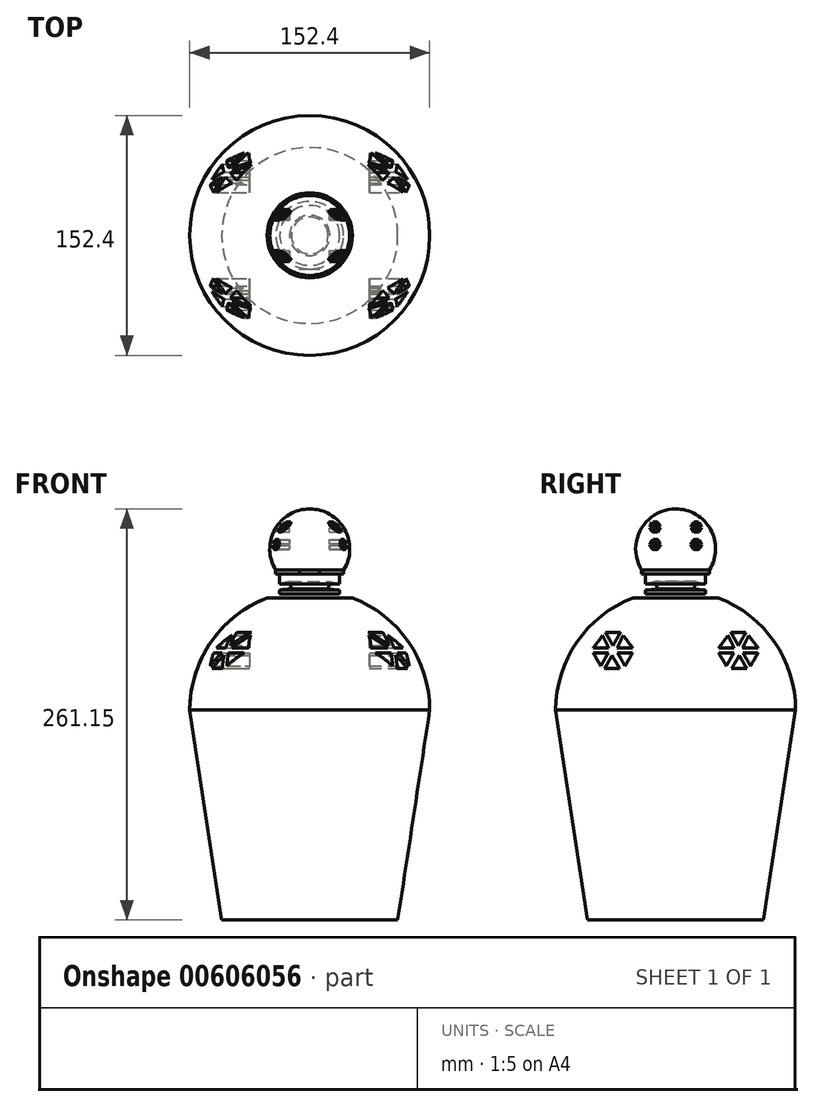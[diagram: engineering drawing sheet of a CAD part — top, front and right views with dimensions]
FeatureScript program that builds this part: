
annotation { "Feature Type Name" : "Feature", "Feature Type Description" : "" }
export const myFeature = defineFeature(function(context is Context, id is Id, definition is map)
    precondition{}
    {
        {
            var Q0;
            Q0=qCreatedBy(makeId("Right.planeOp"),FACE);
            var sketch = newSketch(context, id + "F0", { "sketchPlane" : qUnion([Q0])});
            skLineSegment(sketch, "E0", {"start": v(0, 0) * mm, "end": v(-76.2, 0) * mm});
            skLineSegment(sketch, "E1", {"start": v(0, 0) * mm, "end": v(76.2, 0) * mm});
            skArc(sketch, "E2", {"start": v(76.2, 0) * mm, "mid": v(0, 76.2) * mm, "end": v(-76.2, 0) * mm});
            skLineSegment(sketch, "E3", {"start": v(-19.05, 73.78) * mm, "end": v(19.05, 73.78) * mm});
            skLineSegment(sketch, "E4", {"start": v(-19.05, 73.78) * mm, "end": v(-19.05, 86.48) * mm});
            skLineSegment(sketch, "E5", {"start": v(-19.05, 86.48) * mm, "end": v(19.05, 86.48) * mm});
            skLineSegment(sketch, "E6", {"start": v(19.05, 86.48) * mm, "end": v(19.05, 73.78) * mm});
            skLineSegment(sketch, "E7", {"start": v(-19.05, 80.13) * mm, "end": v(-19.05, 76.32) * mm});
            skLineSegment(sketch, "E8", {"start": v(-19.05, 86.48) * mm, "end": v(-21.6, 86.48) * mm});
            skLineSegment(sketch, "E9", {"start": v(-21.6, 86.48) * mm, "end": v(-21.6, 89.02) * mm});
            skLineSegment(sketch, "E10", {"start": v(-21.6, 89.02) * mm, "end": v(21.59, 89.02) * mm});
            skLineSegment(sketch, "E11", {"start": v(21.59, 89.02) * mm, "end": v(21.59, 86.48) * mm});
            skLineSegment(sketch, "E12", {"start": v(21.59, 86.48) * mm, "end": v(19.05, 86.48) * mm});
            skArc(sketch, "E13", {"start": v(21.59, 89.02) * mm, "mid": v(0, 127.8) * mm, "end": v(-21.6, 89.02) * mm});
            skFitSpline(sketch, "E14", {"points": [v(-19.05, 80.13) * mm, v(-35.52, 80.13) * mm, v(-45.74, 88.7) * mm, v(-45.02, 104.83) * mm, v(-33.36, 105.83) * mm, v(-27.32, 90.87) * mm, v(-21.6, 86.48) * mm], "startDerivative": vector(-93.4, -10.6) * mm, "endDerivative": vector(53.06, -21.54) * mm});
            skFitSpline(sketch, "E15", {"points": [v(-19.05, 76.32) * mm, v(-39.12, 76.32) * mm, v(-50.81, 89.03) * mm, v(-48.47, 106.7) * mm, v(-31.02, 109.62) * mm, v(-26.22, 94.73) * mm, v(-21.6, 89.02) * mm], "startDerivative": vector(-113.52, -14.07) * mm, "endDerivative": vector(62.51, -36.47) * mm});
            skLineSegment(sketch, "E16", {"start": v(-27.04, 71.24) * mm, "end": v(27.04, 71.24) * mm});
            skLineSegment(sketch, "E17", {"start": v(0, 0) * mm, "end": v(0, 127.8) * mm});
            skLineSegment(sketch, "E18", {"start": v(-19.05, 80.13) * mm, "end": v(-12.8, 81.65) * mm});
            skLineSegment(sketch, "E19", {"start": v(-12.8, 81.65) * mm, "end": v(-11.67, 77) * mm});
            skLineSegment(sketch, "E20", {"start": v(-11.67, 77) * mm, "end": v(-19.05, 76.32) * mm});
            skLineSegment(sketch, "E21", {"start": v(-21.6, 89.02) * mm, "end": v(-16.42, 87.75) * mm});
            skPoint(sketch, "E21.endSnap0", {"position": v(-21.6, 87.75) * mm});
            skLineSegment(sketch, "E22", {"start": v(-16.42, 87.75) * mm, "end": v(-21.6, 86.48) * mm});
            skSolve(sketch);
        }
        {
            var Q0;
            {var subQ0=sQuery(id+"F0.wireOp",EDGE,"E0");Q0=makeQuery(id+"F0.imprint","IMPRINT",FACE,{"disambiguationData":[TD([[makeQuery(id+"F0.imprint","IMPRINT",EDGE,{"derivedFrom":subQ0}),-1.0]])]});}
            var Q1;
            {var subQ0=sQuery(id+"F0.wireOp",EDGE,"E13");var subQ3=sQuery(id+"F0.wireOp",EDGE,"E17");var subQ5=makeQuery(id+"F0.imprint","INTERSECT",VERTEX,{"derivedFrom":[subQ0,subQ3]});Q1=makeQuery(id+"F0.imprint","IMPRINT",FACE,{"disambiguationData":[TD([[makeQuery(id+"F0.imprint","IMPRINT",EDGE,{"disambiguationData":[TD([[subQ5,1.0]])],"derivedFrom":subQ3}),1.0]])]});}
            var Q2;
            {var subQ1=sQuery(id+"F0.wireOp",EDGE,"E2");var subQ3=sQuery(id+"F0.wireOp",EDGE,"E17");var subQ4=makeQuery(id+"F0.imprint","INTERSECT",VERTEX,{"derivedFrom":[subQ1,subQ3]});Q2=makeQuery(id+"F0.imprint","IMPRINT",FACE,{"disambiguationData":[TD([[makeQuery(id+"F0.imprint","IMPRINT",EDGE,{"disambiguationData":[TD([[subQ4,1.0]])],"derivedFrom":subQ3}),1.0]])]});}
            var Q3;
            {var subQ1=sQuery(id+"F0.wireOp",EDGE,"E2");var subQ3=sQuery(id+"F0.wireOp",EDGE,"E16");var subQ4=makeQuery(id+"F0.imprint","INTERSECT",VERTEX,{"disambiguationData":[OD(0.0)],"derivedFrom":[subQ1,subQ3]});Q3=makeQuery(id+"F0.imprint","IMPRINT",FACE,{"disambiguationData":[TD([[makeQuery(id+"F0.imprint","IMPRINT",EDGE,{"disambiguationData":[TD([[subQ4,-1.0]])],"derivedFrom":subQ3}),1.0]])]});}
            var Q4;
            {var subQ4=sQuery(id+"F0.wireOp",EDGE,"E8");Q4=makeQuery(id+"F0.imprint","IMPRINT",FACE,{"disambiguationData":[TD([[makeQuery(id+"F0.imprint","IMPRINT",EDGE,{"derivedFrom":subQ4}),-1.0]])]});}
            var Q5;
            {var subQ5=sQuery(id+"F0.wireOp",EDGE,"E18");Q5=makeQuery(id+"F0.imprint","IMPRINT",FACE,{"disambiguationData":[TD([[makeQuery(id+"F0.imprint","IMPRINT",EDGE,{"derivedFrom":subQ5}),1.0]])]});}
            var Q6;
            Q6=makeQuery(id+"F0.imprint","IMPRINT",FACE,{"disambiguationData":[TD([[makeQuery(id+"F0.imprint","IMPRINT",EDGE,{"derivedFrom":sQuery(id+"F0.wireOp",EDGE,"E7")}),1.0]])]});
            var Q7;
            Q7=makeQuery(id+"F0.imprint","IMPRINT",FACE,{"disambiguationData":[TD([[makeQuery(id+"F0.imprint","IMPRINT",EDGE,{"derivedFrom":sQuery(id+"F0.wireOp",EDGE,"E9")}),-1.0]])]});
            var Q8;
            Q8=sQuery(id+"F0.wireOp",EDGE,"E17");
            revolve(context, id + "F1", {"entities" : qUnion([Q0, Q1, Q2, Q3, Q4, Q5, Q6, Q7]), "axis" : qUnion([Q8]), "revolveType" : RevolveType.FULL});
        }
        {
            var Q0;
            Q0=makeQuery(id+"F0.imprint","IMPRINT",FACE,{"disambiguationData":[TD([[makeQuery(id+"F0.imprint","IMPRINT",EDGE,{"derivedFrom":sQuery(id+"F0.wireOp",EDGE,"E7")}),-1.0]])]});
            var Q1;
            Q1=makeQuery(id+"F0.imprint","IMPRINT",FACE,{"disambiguationData":[TD([[makeQuery(id+"F0.imprint","IMPRINT",EDGE,{"derivedFrom":sQuery(id+"F0.wireOp",EDGE,"E7")}),1.0]])]});
            var Q2;
            Q2=makeQuery(id+"F0.imprint","IMPRINT",FACE,{"disambiguationData":[TD([[makeQuery(id+"F0.imprint","IMPRINT",EDGE,{"derivedFrom":sQuery(id+"F0.wireOp",EDGE,"E9")}),-1.0]])]});
            extrude(context, id + "F2", {"entities" : qUnion([Q0, Q1, Q2]), "operationType" : NewBodyOperationType.ADD, "endBound" : BoundingType.SYMMETRIC, "depth" : 12.7 * mm, "offsetDistance" : 25.4 * mm});
        }
        {
            var Q0;
            Q0=qCreatedBy(makeId("Right.planeOp"),FACE);
            var sketch = newSketch(context, id + "F3", { "sketchPlane" : qUnion([Q0])});
            skLineSegment(sketch, "E23.0", {"start": v(0, 0) * mm, "end": v(-76.2, 0) * mm});
            skLineSegment(sketch, "E23.1", {"start": v(0, 0) * mm, "end": v(76.2, 0) * mm});
            skLineSegment(sketch, "E24", {"start": v(0, 0) * mm, "end": v(0, -133.35) * mm});
            skLineSegment(sketch, "E25", {"start": v(0, -133.35) * mm, "end": v(-55.88, -133.35) * mm});
            skLineSegment(sketch, "E26", {"start": v(-55.88, -133.35) * mm, "end": v(-76.2, 0) * mm});
            skSolve(sketch);
        }
        {
            var Q0;
            Q0 = qSketchRegion(id + "F3", true);
            var Q1;
            Q1=sQuery(id+"F3.wireOp",EDGE,"E24");
            revolve(context, id + "F4", {"entities" : qUnion([Q0]), "axis" : qUnion([Q1]), "revolveType" : RevolveType.FULL});
        }
        {
            var Q0;
            Q0=qCreatedBy(makeId("Right.planeOp"),FACE);
            var sketch = newSketch(context, id + "F5", { "sketchPlane" : qUnion([Q0])});
            skLineSegment(sketch, "E27.0", {"start": v(76.2, 0) * mm, "end": v(-76.2, 0) * mm});
            skLineSegment(sketch, "E28.0", {"start": v(19.05, 73.78) * mm, "end": v(-19.05, 73.78) * mm});
            skLineSegment(sketch, "E29", {"start": v(0, 73.78) * mm, "end": v(0, 0) * mm, "construction": true});
            skLineSegment(sketch, "E30", {"start": v(-45.22, 26.32) * mm, "end": v(-35.57, 26.32) * mm});
            skLineSegment(sketch, "E31", {"start": v(-35.57, 26.32) * mm, "end": v(-40.4, 34.68) * mm});
            skPoint(sketch, "E31.endSnap0", {"position": v(-40.4, 26.32) * mm});
            skLineSegment(sketch, "E32", {"start": v(-40.4, 34.68) * mm, "end": v(-45.22, 26.32) * mm});
            skCircle(sketch, "E33", {"center": v(-39.84, 37.8) * mm, "radius": 3.18 * mm, "construction": true});
            skLineSegment(sketch, "E34", {"start": v(-39.84, 40.98) * mm, "end": v(-44.67, 49.35) * mm});
            skLineSegment(sketch, "E35", {"start": v(-44.67, 49.35) * mm, "end": v(-35.01, 49.35) * mm});
            skLineSegment(sketch, "E36", {"start": v(-35.01, 49.35) * mm, "end": v(-39.84, 40.98) * mm});
            skLineSegment(sketch, "E37", {"start": v(-42.7, 36.43) * mm, "end": v(-47.53, 28.07) * mm});
            skLineSegment(sketch, "E38", {"start": v(-47.53, 28.07) * mm, "end": v(-52.36, 36.43) * mm});
            skLineSegment(sketch, "E39", {"start": v(-52.36, 36.43) * mm, "end": v(-42.7, 36.43) * mm});
            skLineSegment(sketch, "E40", {"start": v(-42.54, 39.48) * mm, "end": v(-52.36, 39.48) * mm});
            skLineSegment(sketch, "E41", {"start": v(-52.36, 39.48) * mm, "end": v(-46.36, 47.41) * mm});
            skLineSegment(sketch, "E42", {"start": v(-46.36, 47.41) * mm, "end": v(-42.54, 39.48) * mm});
            skLineSegment(sketch, "E43.MirrorCS", {"start": v(-36.98, 36.43) * mm, "end": v(-32.15, 28.07) * mm});
            skLineSegment(sketch, "E44.MirrorCS", {"start": v(-32.15, 28.07) * mm, "end": v(-27.32, 36.43) * mm});
            skLineSegment(sketch, "E45.MirrorCS", {"start": v(-27.32, 36.43) * mm, "end": v(-36.98, 36.43) * mm});
            skLineSegment(sketch, "E46.MirrorCS", {"start": v(-37.14, 39.48) * mm, "end": v(-27.32, 39.48) * mm});
            skLineSegment(sketch, "E47.MirrorCS", {"start": v(-33.32, 47.41) * mm, "end": v(-37.14, 39.48) * mm});
            skLineSegment(sketch, "E48.MirrorCS", {"start": v(-27.32, 39.48) * mm, "end": v(-33.32, 47.41) * mm});
            skCircle(sketch, "E49.MirrorC", {"center": v(39.84, 37.8) * mm, "radius": 3.18 * mm, "construction": true});
            skLineSegment(sketch, "E50.MirrorCS", {"start": v(45.22, 26.32) * mm, "end": v(35.57, 26.32) * mm});
            skLineSegment(sketch, "E51.MirrorCS", {"start": v(46.36, 47.41) * mm, "end": v(42.54, 39.48) * mm});
            skLineSegment(sketch, "E52.MirrorCS", {"start": v(37.14, 39.48) * mm, "end": v(27.32, 39.48) * mm});
            skLineSegment(sketch, "E53.MirrorCS", {"start": v(44.67, 49.35) * mm, "end": v(35.01, 49.35) * mm});
            skLineSegment(sketch, "E54.MirrorCS", {"start": v(52.36, 36.43) * mm, "end": v(42.7, 36.43) * mm});
            skLineSegment(sketch, "E55.MirrorCS", {"start": v(39.84, 40.98) * mm, "end": v(44.67, 49.35) * mm});
            skLineSegment(sketch, "E56.MirrorCS", {"start": v(42.54, 39.48) * mm, "end": v(52.36, 39.48) * mm});
            skLineSegment(sketch, "E57.MirrorCS", {"start": v(35.01, 49.35) * mm, "end": v(39.84, 40.98) * mm});
            skLineSegment(sketch, "E58.MirrorCS", {"start": v(42.7, 36.43) * mm, "end": v(47.53, 28.07) * mm});
            skLineSegment(sketch, "E59.MirrorCS", {"start": v(33.32, 47.41) * mm, "end": v(37.14, 39.48) * mm});
            skLineSegment(sketch, "E60.MirrorCS", {"start": v(35.57, 26.32) * mm, "end": v(40.4, 34.68) * mm});
            skLineSegment(sketch, "E61.MirrorCS", {"start": v(47.53, 28.07) * mm, "end": v(52.36, 36.43) * mm});
            skLineSegment(sketch, "E62.MirrorCS", {"start": v(27.32, 36.43) * mm, "end": v(36.98, 36.43) * mm});
            skLineSegment(sketch, "E63.MirrorCS", {"start": v(32.15, 28.07) * mm, "end": v(27.32, 36.43) * mm});
            skLineSegment(sketch, "E64.MirrorCS", {"start": v(27.32, 39.48) * mm, "end": v(33.32, 47.41) * mm});
            skPoint(sketch, "E65.MirrorP", {"position": v(40.4, 26.32) * mm});
            skLineSegment(sketch, "E66.MirrorCS", {"start": v(52.36, 39.48) * mm, "end": v(46.36, 47.41) * mm});
            skLineSegment(sketch, "E67.MirrorCS", {"start": v(40.4, 34.68) * mm, "end": v(45.22, 26.32) * mm});
            skLineSegment(sketch, "E68.MirrorCS", {"start": v(36.98, 36.43) * mm, "end": v(32.15, 28.07) * mm});
            skSolve(sketch);
        }
        {
            var Q0;
            Q0 = qSketchRegion(id + "F5", true);
            extrude(context, id + "F6", {"entities" : qUnion([Q0]), "operationType" : NewBodyOperationType.ADD, "endBound" : BoundingType.SYMMETRIC, "depth" : 101.6 * mm, "offsetDistance" : 25.4 * mm, "hasSecondDirection" : true, "secondDirectionOppositeDirection" : true, "secondDirectionDepth" : 25.4 * mm});
        }
        {
            var Q0;
            Q0 = qSketchRegion(id + "F5", true);
            extrude(context, id + "F7", {"entities" : qUnion([Q0]), "operationType" : NewBodyOperationType.ADD, "endBound" : BoundingType.SYMMETRIC, "depth" : 127 * mm, "offsetDistance" : 25.4 * mm});
        }
        {
            var Q0;
            Q0=makeQuery(id+"F7.opExtrude","CAP_FACE",FACE,{"disambiguationData":[OSD([sQuery(id+"F5.wireOp",EDGE,"E40"),sQuery(id+"F5.wireOp",EDGE,"E41"),sQuery(id+"F5.wireOp",EDGE,"E42")])],"isStart":false});
            var Q1;
            Q1=makeQuery(id+"F7.opExtrude","CAP_FACE",FACE,{"disambiguationData":[OSD([sQuery(id+"F5.wireOp",EDGE,"E34"),sQuery(id+"F5.wireOp",EDGE,"E35"),sQuery(id+"F5.wireOp",EDGE,"E36")])],"isStart":false});
            var Q2;
            Q2=makeQuery(id+"F7.opExtrude","CAP_FACE",FACE,{"disambiguationData":[OSD([sQuery(id+"F5.wireOp",EDGE,"E46.MirrorCS"),sQuery(id+"F5.wireOp",EDGE,"E47.MirrorCS"),sQuery(id+"F5.wireOp",EDGE,"E48.MirrorCS")])],"isStart":false});
            var Q3;
            Q3=makeQuery(id+"F7.opExtrude","CAP_FACE",FACE,{"disambiguationData":[OSD([sQuery(id+"F5.wireOp",EDGE,"E43.MirrorCS"),sQuery(id+"F5.wireOp",EDGE,"E44.MirrorCS"),sQuery(id+"F5.wireOp",EDGE,"E45.MirrorCS")])],"isStart":false});
            var Q4;
            Q4=makeQuery(id+"F7.opExtrude","CAP_FACE",FACE,{"disambiguationData":[OSD([sQuery(id+"F5.wireOp",EDGE,"E30"),sQuery(id+"F5.wireOp",EDGE,"E31"),sQuery(id+"F5.wireOp",EDGE,"E32")])],"isStart":false});
            var Q5;
            Q5=makeQuery(id+"F7.opExtrude","CAP_FACE",FACE,{"disambiguationData":[OSD([sQuery(id+"F5.wireOp",EDGE,"E37"),sQuery(id+"F5.wireOp",EDGE,"E38"),sQuery(id+"F5.wireOp",EDGE,"E39")])],"isStart":false});
            var Q6;
            Q6=makeQuery(id+"F7.opExtrude","CAP_FACE",FACE,{"disambiguationData":[OSD([sQuery(id+"F5.wireOp",EDGE,"E62.MirrorCS"),sQuery(id+"F5.wireOp",EDGE,"E63.MirrorCS"),sQuery(id+"F5.wireOp",EDGE,"E68.MirrorCS")])],"isStart":false});
            var Q7;
            Q7=makeQuery(id+"F7.opExtrude","CAP_FACE",FACE,{"disambiguationData":[OSD([sQuery(id+"F5.wireOp",EDGE,"E52.MirrorCS"),sQuery(id+"F5.wireOp",EDGE,"E59.MirrorCS"),sQuery(id+"F5.wireOp",EDGE,"E64.MirrorCS")])],"isStart":false});
            var Q8;
            Q8=makeQuery(id+"F7.opExtrude","CAP_FACE",FACE,{"disambiguationData":[OSD([sQuery(id+"F5.wireOp",EDGE,"E53.MirrorCS"),sQuery(id+"F5.wireOp",EDGE,"E55.MirrorCS"),sQuery(id+"F5.wireOp",EDGE,"E57.MirrorCS")])],"isStart":false});
            var Q9;
            Q9=makeQuery(id+"F7.opExtrude","CAP_FACE",FACE,{"disambiguationData":[OSD([sQuery(id+"F5.wireOp",EDGE,"E51.MirrorCS"),sQuery(id+"F5.wireOp",EDGE,"E56.MirrorCS"),sQuery(id+"F5.wireOp",EDGE,"E66.MirrorCS")])],"isStart":false});
            var Q10;
            Q10=makeQuery(id+"F7.opExtrude","CAP_FACE",FACE,{"disambiguationData":[OSD([sQuery(id+"F5.wireOp",EDGE,"E54.MirrorCS"),sQuery(id+"F5.wireOp",EDGE,"E58.MirrorCS"),sQuery(id+"F5.wireOp",EDGE,"E61.MirrorCS")])],"isStart":false});
            var Q11;
            Q11=makeQuery(id+"F7.opExtrude","CAP_FACE",FACE,{"disambiguationData":[OSD([sQuery(id+"F5.wireOp",EDGE,"E50.MirrorCS"),sQuery(id+"F5.wireOp",EDGE,"E60.MirrorCS"),sQuery(id+"F5.wireOp",EDGE,"E67.MirrorCS")])],"isStart":false});
            var Q12;
            Q12=makeQuery(id+"F7.opExtrude","CAP_FACE",FACE,{"disambiguationData":[OSD([sQuery(id+"F5.wireOp",EDGE,"E51.MirrorCS"),sQuery(id+"F5.wireOp",EDGE,"E56.MirrorCS"),sQuery(id+"F5.wireOp",EDGE,"E66.MirrorCS")])],"isStart":true});
            var Q13;
            Q13=makeQuery(id+"F7.opExtrude","CAP_FACE",FACE,{"disambiguationData":[OSD([sQuery(id+"F5.wireOp",EDGE,"E54.MirrorCS"),sQuery(id+"F5.wireOp",EDGE,"E58.MirrorCS"),sQuery(id+"F5.wireOp",EDGE,"E61.MirrorCS")])],"isStart":true});
            var Q14;
            Q14=makeQuery(id+"F7.opExtrude","CAP_FACE",FACE,{"disambiguationData":[OSD([sQuery(id+"F5.wireOp",EDGE,"E50.MirrorCS"),sQuery(id+"F5.wireOp",EDGE,"E60.MirrorCS"),sQuery(id+"F5.wireOp",EDGE,"E67.MirrorCS")])],"isStart":true});
            var Q15;
            Q15=makeQuery(id+"F7.opExtrude","CAP_FACE",FACE,{"disambiguationData":[OSD([sQuery(id+"F5.wireOp",EDGE,"E62.MirrorCS"),sQuery(id+"F5.wireOp",EDGE,"E63.MirrorCS"),sQuery(id+"F5.wireOp",EDGE,"E68.MirrorCS")])],"isStart":true});
            var Q16;
            Q16=makeQuery(id+"F7.opExtrude","CAP_FACE",FACE,{"disambiguationData":[OSD([sQuery(id+"F5.wireOp",EDGE,"E52.MirrorCS"),sQuery(id+"F5.wireOp",EDGE,"E59.MirrorCS"),sQuery(id+"F5.wireOp",EDGE,"E64.MirrorCS")])],"isStart":true});
            var Q17;
            Q17=makeQuery(id+"F7.opExtrude","CAP_FACE",FACE,{"disambiguationData":[OSD([sQuery(id+"F5.wireOp",EDGE,"E53.MirrorCS"),sQuery(id+"F5.wireOp",EDGE,"E55.MirrorCS"),sQuery(id+"F5.wireOp",EDGE,"E57.MirrorCS")])],"isStart":true});
            var Q18;
            Q18=makeQuery(id+"F7.opExtrude","CAP_FACE",FACE,{"disambiguationData":[OSD([sQuery(id+"F5.wireOp",EDGE,"E43.MirrorCS"),sQuery(id+"F5.wireOp",EDGE,"E44.MirrorCS"),sQuery(id+"F5.wireOp",EDGE,"E45.MirrorCS")])],"isStart":true});
            var Q19;
            Q19=makeQuery(id+"F7.opExtrude","CAP_FACE",FACE,{"disambiguationData":[OSD([sQuery(id+"F5.wireOp",EDGE,"E30"),sQuery(id+"F5.wireOp",EDGE,"E31"),sQuery(id+"F5.wireOp",EDGE,"E32")])],"isStart":true});
            var Q20;
            Q20=makeQuery(id+"F7.opExtrude","CAP_FACE",FACE,{"disambiguationData":[OSD([sQuery(id+"F5.wireOp",EDGE,"E37"),sQuery(id+"F5.wireOp",EDGE,"E38"),sQuery(id+"F5.wireOp",EDGE,"E39")])],"isStart":true});
            var Q21;
            Q21=makeQuery(id+"F7.opExtrude","CAP_FACE",FACE,{"disambiguationData":[OSD([sQuery(id+"F5.wireOp",EDGE,"E40"),sQuery(id+"F5.wireOp",EDGE,"E41"),sQuery(id+"F5.wireOp",EDGE,"E42")])],"isStart":true});
            var Q22;
            Q22=makeQuery(id+"F7.opExtrude","CAP_FACE",FACE,{"disambiguationData":[OSD([sQuery(id+"F5.wireOp",EDGE,"E34"),sQuery(id+"F5.wireOp",EDGE,"E35"),sQuery(id+"F5.wireOp",EDGE,"E36")])],"isStart":true});
            var Q23;
            Q23=makeQuery(id+"F7.opExtrude","CAP_FACE",FACE,{"disambiguationData":[OSD([sQuery(id+"F5.wireOp",EDGE,"E46.MirrorCS"),sQuery(id+"F5.wireOp",EDGE,"E47.MirrorCS"),sQuery(id+"F5.wireOp",EDGE,"E48.MirrorCS")])],"isStart":true});
            extrude(context, id + "F8", {"entities" : qUnion([Q0, Q1, Q2, Q3, Q4, Q5, Q6, Q7, Q8, Q9, Q10, Q11, Q12, Q13, Q14, Q15, Q16, Q17, Q18, Q19, Q20, Q21, Q22, Q23]), "operationType" : NewBodyOperationType.REMOVE, "oppositeDirection" : true, "depth" : 25.4 * mm, "offsetDistance" : 25.4 * mm, "hasSecondDirection" : true, "secondDirectionOppositeDirection" : false, "secondDirectionDepth" : 25.4 * mm});
        }
        {
            var Q0;
            Q0=qCreatedBy(makeId("Right.planeOp"),FACE);
            var sketch = newSketch(context, id + "F9", { "sketchPlane" : qUnion([Q0])});
            skLineSegment(sketch, "E69.0", {"start": v(21.59, 89.02) * mm, "end": v(-21.6, 89.02) * mm});
            skLineSegment(sketch, "E70", {"start": v(0, 89.02) * mm, "end": v(0, 127.8) * mm, "construction": true});
            skLineSegment(sketch, "E71", {"start": v(-13.1, 116.83) * mm, "end": v(-14.54, 119.33) * mm});
            skLineSegment(sketch, "E72", {"start": v(-14.54, 119.33) * mm, "end": v(-11.65, 119.33) * mm});
            skLineSegment(sketch, "E73", {"start": v(-11.65, 119.33) * mm, "end": v(-13.1, 116.83) * mm});
            skLineSegment(sketch, "E74", {"start": v(-13.1, 115.56) * mm, "end": v(-14.54, 113.05) * mm});
            skLineSegment(sketch, "E75", {"start": v(-14.54, 113.05) * mm, "end": v(-11.65, 113.05) * mm});
            skLineSegment(sketch, "E76", {"start": v(-11.65, 113.05) * mm, "end": v(-13.1, 115.56) * mm});
            skLineSegment(sketch, "E77", {"start": v(-13.58, 115.79) * mm, "end": v(-15.03, 113.28) * mm});
            skLineSegment(sketch, "E78", {"start": v(-15.03, 113.28) * mm, "end": v(-16.47, 115.79) * mm});
            skLineSegment(sketch, "E79", {"start": v(-16.47, 115.79) * mm, "end": v(-13.58, 115.79) * mm});
            skLineSegment(sketch, "E80", {"start": v(-13.58, 116.6) * mm, "end": v(-16.47, 116.6) * mm});
            skLineSegment(sketch, "E81", {"start": v(-16.47, 116.6) * mm, "end": v(-15.03, 119.1) * mm});
            skLineSegment(sketch, "E82", {"start": v(-15.03, 119.1) * mm, "end": v(-13.58, 116.6) * mm});
            skPoint(sketch, "E83.endSnap0", {"position": v(-13.1, 113.05) * mm});
            skLineSegment(sketch, "E84.MirrorCS", {"start": v(-11.16, 119.1) * mm, "end": v(-12.6, 116.6) * mm});
            skLineSegment(sketch, "E85.MirrorCS", {"start": v(-9.71, 116.6) * mm, "end": v(-11.16, 119.1) * mm});
            skLineSegment(sketch, "E86.MirrorCS", {"start": v(-12.6, 116.6) * mm, "end": v(-9.71, 116.6) * mm});
            skLineSegment(sketch, "E87.MirrorCS", {"start": v(-9.71, 115.79) * mm, "end": v(-12.6, 115.79) * mm});
            skLineSegment(sketch, "E88.MirrorCS", {"start": v(-12.6, 115.79) * mm, "end": v(-11.16, 113.28) * mm});
            skLineSegment(sketch, "E89.MirrorCS", {"start": v(-11.16, 113.28) * mm, "end": v(-9.71, 115.79) * mm});
            skLineSegment(sketch, "E90.MirrorCS", {"start": v(-14.54, 108.27) * mm, "end": v(-11.65, 108.27) * mm});
            skLineSegment(sketch, "E91.MirrorCS", {"start": v(-15.03, 108.04) * mm, "end": v(-16.47, 105.54) * mm});
            skLineSegment(sketch, "E92.MirrorCS", {"start": v(-13.58, 105.54) * mm, "end": v(-15.03, 108.04) * mm});
            skLineSegment(sketch, "E93.MirrorCS", {"start": v(-13.1, 105.77) * mm, "end": v(-14.54, 108.27) * mm});
            skLineSegment(sketch, "E94.MirrorCS", {"start": v(-11.65, 108.27) * mm, "end": v(-13.1, 105.77) * mm});
            skLineSegment(sketch, "E95.MirrorCS", {"start": v(-16.47, 105.54) * mm, "end": v(-13.58, 105.54) * mm});
            skLineSegment(sketch, "E96.MirrorCS", {"start": v(-12.6, 105.54) * mm, "end": v(-11.16, 108.04) * mm});
            skLineSegment(sketch, "E97.MirrorCS", {"start": v(-11.16, 108.04) * mm, "end": v(-9.71, 105.54) * mm});
            skLineSegment(sketch, "E98.MirrorCS", {"start": v(-9.71, 105.54) * mm, "end": v(-12.6, 105.54) * mm});
            skLineSegment(sketch, "E99.MirrorCS", {"start": v(-12.6, 104.73) * mm, "end": v(-9.71, 104.73) * mm});
            skLineSegment(sketch, "E100.MirrorCS", {"start": v(-9.71, 104.73) * mm, "end": v(-11.16, 102.22) * mm});
            skLineSegment(sketch, "E101.MirrorCS", {"start": v(-11.16, 102.22) * mm, "end": v(-12.6, 104.73) * mm});
            skLineSegment(sketch, "E102.MirrorCS", {"start": v(-11.65, 102) * mm, "end": v(-13.1, 104.5) * mm});
            skLineSegment(sketch, "E103.MirrorCS", {"start": v(-14.54, 102) * mm, "end": v(-11.65, 102) * mm});
            skLineSegment(sketch, "E104.MirrorCS", {"start": v(-13.1, 104.5) * mm, "end": v(-14.54, 102) * mm});
            skLineSegment(sketch, "E105.MirrorCS", {"start": v(-15.03, 102.22) * mm, "end": v(-13.58, 104.73) * mm});
            skLineSegment(sketch, "E106.MirrorCS", {"start": v(-13.58, 104.73) * mm, "end": v(-16.47, 104.73) * mm});
            skLineSegment(sketch, "E107.MirrorCS", {"start": v(-16.47, 104.73) * mm, "end": v(-15.03, 102.22) * mm});
            skLineSegment(sketch, "E108.MirrorCS", {"start": v(11.65, 113.05) * mm, "end": v(13.1, 115.56) * mm});
            skLineSegment(sketch, "E109.MirrorCS", {"start": v(13.1, 115.56) * mm, "end": v(14.54, 113.05) * mm});
            skLineSegment(sketch, "E110.MirrorCS", {"start": v(14.54, 113.05) * mm, "end": v(11.65, 113.05) * mm});
            skLineSegment(sketch, "E111.MirrorCS", {"start": v(11.65, 102) * mm, "end": v(13.1, 104.5) * mm});
            skLineSegment(sketch, "E112.MirrorCS", {"start": v(9.71, 116.6) * mm, "end": v(11.16, 119.1) * mm});
            skLineSegment(sketch, "E113.MirrorCS", {"start": v(12.6, 115.79) * mm, "end": v(11.16, 113.28) * mm});
            skLineSegment(sketch, "E114.MirrorCS", {"start": v(15.03, 119.1) * mm, "end": v(13.58, 116.6) * mm});
            skLineSegment(sketch, "E115.MirrorCS", {"start": v(15.03, 108.04) * mm, "end": v(16.47, 105.54) * mm});
            skLineSegment(sketch, "E116.MirrorCS", {"start": v(16.47, 104.73) * mm, "end": v(15.03, 102.22) * mm});
            skLineSegment(sketch, "E117.MirrorCS", {"start": v(13.1, 116.83) * mm, "end": v(14.54, 119.33) * mm});
            skLineSegment(sketch, "E118.MirrorCS", {"start": v(11.16, 113.28) * mm, "end": v(9.71, 115.79) * mm});
            skLineSegment(sketch, "E119.MirrorCS", {"start": v(16.47, 115.79) * mm, "end": v(13.58, 115.79) * mm});
            skPoint(sketch, "E120.MirrorP", {"position": v(13.1, 113.05) * mm});
            skLineSegment(sketch, "E121.MirrorCS", {"start": v(12.6, 105.54) * mm, "end": v(11.16, 108.04) * mm});
            skLineSegment(sketch, "E122.MirrorCS", {"start": v(13.58, 104.73) * mm, "end": v(16.47, 104.73) * mm});
            skLineSegment(sketch, "E123.MirrorCS", {"start": v(11.16, 108.04) * mm, "end": v(9.71, 105.54) * mm});
            skLineSegment(sketch, "E124.MirrorCS", {"start": v(11.16, 119.1) * mm, "end": v(12.6, 116.6) * mm});
            skLineSegment(sketch, "E125.MirrorCS", {"start": v(16.47, 105.54) * mm, "end": v(13.58, 105.54) * mm});
            skLineSegment(sketch, "E126.MirrorCS", {"start": v(9.71, 104.73) * mm, "end": v(11.16, 102.22) * mm});
            skLineSegment(sketch, "E127.MirrorCS", {"start": v(14.54, 108.27) * mm, "end": v(11.65, 108.27) * mm});
            skLineSegment(sketch, "E128.MirrorCS", {"start": v(9.71, 115.79) * mm, "end": v(12.6, 115.79) * mm});
            skLineSegment(sketch, "E129.MirrorCS", {"start": v(13.58, 115.79) * mm, "end": v(15.03, 113.28) * mm});
            skLineSegment(sketch, "E130.MirrorCS", {"start": v(14.54, 119.33) * mm, "end": v(11.65, 119.33) * mm});
            skLineSegment(sketch, "E131.MirrorCS", {"start": v(11.16, 102.22) * mm, "end": v(12.6, 104.73) * mm});
            skLineSegment(sketch, "E132.MirrorCS", {"start": v(14.54, 102) * mm, "end": v(11.65, 102) * mm});
            skLineSegment(sketch, "E133.MirrorCS", {"start": v(12.6, 104.73) * mm, "end": v(9.71, 104.73) * mm});
            skLineSegment(sketch, "E134.MirrorCS", {"start": v(15.03, 102.22) * mm, "end": v(13.58, 104.73) * mm});
            skLineSegment(sketch, "E135.MirrorCS", {"start": v(11.65, 108.27) * mm, "end": v(13.1, 105.77) * mm});
            skLineSegment(sketch, "E136.MirrorCS", {"start": v(16.47, 116.6) * mm, "end": v(15.03, 119.1) * mm});
            skLineSegment(sketch, "E137.MirrorCS", {"start": v(13.58, 116.6) * mm, "end": v(16.47, 116.6) * mm});
            skLineSegment(sketch, "E138.MirrorCS", {"start": v(12.6, 116.6) * mm, "end": v(9.71, 116.6) * mm});
            skLineSegment(sketch, "E139.MirrorCS", {"start": v(15.03, 113.28) * mm, "end": v(16.47, 115.79) * mm});
            skLineSegment(sketch, "E140.MirrorCS", {"start": v(11.65, 119.33) * mm, "end": v(13.1, 116.83) * mm});
            skLineSegment(sketch, "E141.MirrorCS", {"start": v(13.1, 104.5) * mm, "end": v(14.54, 102) * mm});
            skLineSegment(sketch, "E142.MirrorCS", {"start": v(13.1, 105.77) * mm, "end": v(14.54, 108.27) * mm});
            skLineSegment(sketch, "E143.MirrorCS", {"start": v(13.58, 105.54) * mm, "end": v(15.03, 108.04) * mm});
            skLineSegment(sketch, "E144.MirrorCS", {"start": v(9.71, 105.54) * mm, "end": v(12.6, 105.54) * mm});
            skSolve(sketch);
        }
        {
            var Q0;
            Q0 = qSketchRegion(id + "F9", true);
            extrude(context, id + "F10", {"entities" : qUnion([Q0]), "operationType" : NewBodyOperationType.ADD, "endBound" : BoundingType.SYMMETRIC, "depth" : 50.8 * mm, "offsetDistance" : 25.4 * mm});
        }
        {
            var Q0;
            Q0=makeQuery(id+"F10.opExtrude","CAP_FACE",FACE,{"disambiguationData":[OSD([sQuery(id+"F9.wireOp",EDGE,"E80"),sQuery(id+"F9.wireOp",EDGE,"E81"),sQuery(id+"F9.wireOp",EDGE,"E82")])],"isStart":false});
            var Q1;
            Q1=makeQuery(id+"F10.opExtrude","CAP_FACE",FACE,{"disambiguationData":[OSD([sQuery(id+"F9.wireOp",EDGE,"E71"),sQuery(id+"F9.wireOp",EDGE,"E72"),sQuery(id+"F9.wireOp",EDGE,"E73")])],"isStart":false});
            var Q2;
            Q2=makeQuery(id+"F10.opExtrude","CAP_FACE",FACE,{"disambiguationData":[OSD([sQuery(id+"F9.wireOp",EDGE,"E84.MirrorCS"),sQuery(id+"F9.wireOp",EDGE,"E85.MirrorCS"),sQuery(id+"F9.wireOp",EDGE,"E86.MirrorCS")])],"isStart":false});
            var Q3;
            Q3=makeQuery(id+"F10.opExtrude","CAP_FACE",FACE,{"disambiguationData":[OSD([sQuery(id+"F9.wireOp",EDGE,"E87.MirrorCS"),sQuery(id+"F9.wireOp",EDGE,"E88.MirrorCS"),sQuery(id+"F9.wireOp",EDGE,"E89.MirrorCS")])],"isStart":false});
            var Q4;
            Q4=makeQuery(id+"F10.opExtrude","CAP_FACE",FACE,{"disambiguationData":[OSD([sQuery(id+"F9.wireOp",EDGE,"E74"),sQuery(id+"F9.wireOp",EDGE,"E75"),sQuery(id+"F9.wireOp",EDGE,"E76")])],"isStart":false});
            var Q5;
            Q5=makeQuery(id+"F10.opExtrude","CAP_FACE",FACE,{"disambiguationData":[OSD([sQuery(id+"F9.wireOp",EDGE,"E77"),sQuery(id+"F9.wireOp",EDGE,"E78"),sQuery(id+"F9.wireOp",EDGE,"E79")])],"isStart":false});
            var Q6;
            Q6=makeQuery(id+"F10.opExtrude","CAP_FACE",FACE,{"disambiguationData":[OSD([sQuery(id+"F9.wireOp",EDGE,"E105.MirrorCS"),sQuery(id+"F9.wireOp",EDGE,"E106.MirrorCS"),sQuery(id+"F9.wireOp",EDGE,"E107.MirrorCS")])],"isStart":false});
            var Q7;
            Q7=makeQuery(id+"F10.opExtrude","CAP_FACE",FACE,{"disambiguationData":[OSD([sQuery(id+"F9.wireOp",EDGE,"E91.MirrorCS"),sQuery(id+"F9.wireOp",EDGE,"E92.MirrorCS"),sQuery(id+"F9.wireOp",EDGE,"E95.MirrorCS")])],"isStart":false});
            var Q8;
            Q8=makeQuery(id+"F10.opExtrude","CAP_FACE",FACE,{"disambiguationData":[OSD([sQuery(id+"F9.wireOp",EDGE,"E90.MirrorCS"),sQuery(id+"F9.wireOp",EDGE,"E93.MirrorCS"),sQuery(id+"F9.wireOp",EDGE,"E94.MirrorCS")])],"isStart":false});
            var Q9;
            Q9=makeQuery(id+"F10.opExtrude","CAP_FACE",FACE,{"disambiguationData":[OSD([sQuery(id+"F9.wireOp",EDGE,"E96.MirrorCS"),sQuery(id+"F9.wireOp",EDGE,"E97.MirrorCS"),sQuery(id+"F9.wireOp",EDGE,"E98.MirrorCS")])],"isStart":false});
            var Q10;
            Q10=makeQuery(id+"F10.opExtrude","CAP_FACE",FACE,{"disambiguationData":[OSD([sQuery(id+"F9.wireOp",EDGE,"E99.MirrorCS"),sQuery(id+"F9.wireOp",EDGE,"E100.MirrorCS"),sQuery(id+"F9.wireOp",EDGE,"E101.MirrorCS")])],"isStart":false});
            var Q11;
            Q11=makeQuery(id+"F10.opExtrude","CAP_FACE",FACE,{"disambiguationData":[OSD([sQuery(id+"F9.wireOp",EDGE,"E102.MirrorCS"),sQuery(id+"F9.wireOp",EDGE,"E103.MirrorCS"),sQuery(id+"F9.wireOp",EDGE,"E104.MirrorCS")])],"isStart":false});
            var Q12;
            Q12=makeQuery(id+"F10.opExtrude","CAP_FACE",FACE,{"disambiguationData":[OSD([sQuery(id+"F9.wireOp",EDGE,"E126.MirrorCS"),sQuery(id+"F9.wireOp",EDGE,"E131.MirrorCS"),sQuery(id+"F9.wireOp",EDGE,"E133.MirrorCS")])],"isStart":false});
            var Q13;
            Q13=makeQuery(id+"F10.opExtrude","CAP_FACE",FACE,{"disambiguationData":[OSD([sQuery(id+"F9.wireOp",EDGE,"E111.MirrorCS"),sQuery(id+"F9.wireOp",EDGE,"E132.MirrorCS"),sQuery(id+"F9.wireOp",EDGE,"E141.MirrorCS")])],"isStart":false});
            var Q14;
            Q14=makeQuery(id+"F10.opExtrude","CAP_FACE",FACE,{"disambiguationData":[OSD([sQuery(id+"F9.wireOp",EDGE,"E116.MirrorCS"),sQuery(id+"F9.wireOp",EDGE,"E122.MirrorCS"),sQuery(id+"F9.wireOp",EDGE,"E134.MirrorCS")])],"isStart":false});
            var Q15;
            Q15=makeQuery(id+"F10.opExtrude","CAP_FACE",FACE,{"disambiguationData":[OSD([sQuery(id+"F9.wireOp",EDGE,"E115.MirrorCS"),sQuery(id+"F9.wireOp",EDGE,"E125.MirrorCS"),sQuery(id+"F9.wireOp",EDGE,"E143.MirrorCS")])],"isStart":false});
            var Q16;
            Q16=makeQuery(id+"F10.opExtrude","CAP_FACE",FACE,{"disambiguationData":[OSD([sQuery(id+"F9.wireOp",EDGE,"E127.MirrorCS"),sQuery(id+"F9.wireOp",EDGE,"E135.MirrorCS"),sQuery(id+"F9.wireOp",EDGE,"E142.MirrorCS")])],"isStart":false});
            var Q17;
            Q17=makeQuery(id+"F10.opExtrude","CAP_FACE",FACE,{"disambiguationData":[OSD([sQuery(id+"F9.wireOp",EDGE,"E121.MirrorCS"),sQuery(id+"F9.wireOp",EDGE,"E123.MirrorCS"),sQuery(id+"F9.wireOp",EDGE,"E144.MirrorCS")])],"isStart":false});
            var Q18;
            Q18=makeQuery(id+"F10.opExtrude","CAP_FACE",FACE,{"disambiguationData":[OSD([sQuery(id+"F9.wireOp",EDGE,"E113.MirrorCS"),sQuery(id+"F9.wireOp",EDGE,"E118.MirrorCS"),sQuery(id+"F9.wireOp",EDGE,"E128.MirrorCS")])],"isStart":false});
            var Q19;
            Q19=makeQuery(id+"F10.opExtrude","CAP_FACE",FACE,{"disambiguationData":[OSD([sQuery(id+"F9.wireOp",EDGE,"E108.MirrorCS"),sQuery(id+"F9.wireOp",EDGE,"E109.MirrorCS"),sQuery(id+"F9.wireOp",EDGE,"E110.MirrorCS")])],"isStart":false});
            var Q20;
            Q20=makeQuery(id+"F10.opExtrude","CAP_FACE",FACE,{"disambiguationData":[OSD([sQuery(id+"F9.wireOp",EDGE,"E119.MirrorCS"),sQuery(id+"F9.wireOp",EDGE,"E129.MirrorCS"),sQuery(id+"F9.wireOp",EDGE,"E139.MirrorCS")])],"isStart":false});
            var Q21;
            Q21=makeQuery(id+"F10.opExtrude","CAP_FACE",FACE,{"disambiguationData":[OSD([sQuery(id+"F9.wireOp",EDGE,"E114.MirrorCS"),sQuery(id+"F9.wireOp",EDGE,"E136.MirrorCS"),sQuery(id+"F9.wireOp",EDGE,"E137.MirrorCS")])],"isStart":false});
            var Q22;
            Q22=makeQuery(id+"F10.opExtrude","CAP_FACE",FACE,{"disambiguationData":[OSD([sQuery(id+"F9.wireOp",EDGE,"E117.MirrorCS"),sQuery(id+"F9.wireOp",EDGE,"E130.MirrorCS"),sQuery(id+"F9.wireOp",EDGE,"E140.MirrorCS")])],"isStart":false});
            var Q23;
            Q23=makeQuery(id+"F10.opExtrude","CAP_FACE",FACE,{"disambiguationData":[OSD([sQuery(id+"F9.wireOp",EDGE,"E112.MirrorCS"),sQuery(id+"F9.wireOp",EDGE,"E124.MirrorCS"),sQuery(id+"F9.wireOp",EDGE,"E138.MirrorCS")])],"isStart":false});
            var Q24;
            Q24=makeQuery(id+"F10.opExtrude","CAP_FACE",FACE,{"disambiguationData":[OSD([sQuery(id+"F9.wireOp",EDGE,"E119.MirrorCS"),sQuery(id+"F9.wireOp",EDGE,"E129.MirrorCS"),sQuery(id+"F9.wireOp",EDGE,"E139.MirrorCS")])],"isStart":true});
            var Q25;
            Q25=makeQuery(id+"F10.opExtrude","CAP_FACE",FACE,{"disambiguationData":[OSD([sQuery(id+"F9.wireOp",EDGE,"E108.MirrorCS"),sQuery(id+"F9.wireOp",EDGE,"E109.MirrorCS"),sQuery(id+"F9.wireOp",EDGE,"E110.MirrorCS")])],"isStart":true});
            var Q26;
            Q26=makeQuery(id+"F10.opExtrude","CAP_FACE",FACE,{"disambiguationData":[OSD([sQuery(id+"F9.wireOp",EDGE,"E113.MirrorCS"),sQuery(id+"F9.wireOp",EDGE,"E118.MirrorCS"),sQuery(id+"F9.wireOp",EDGE,"E128.MirrorCS")])],"isStart":true});
            var Q27;
            Q27=makeQuery(id+"F10.opExtrude","CAP_FACE",FACE,{"disambiguationData":[OSD([sQuery(id+"F9.wireOp",EDGE,"E114.MirrorCS"),sQuery(id+"F9.wireOp",EDGE,"E136.MirrorCS"),sQuery(id+"F9.wireOp",EDGE,"E137.MirrorCS")])],"isStart":true});
            var Q28;
            Q28=makeQuery(id+"F10.opExtrude","CAP_FACE",FACE,{"disambiguationData":[OSD([sQuery(id+"F9.wireOp",EDGE,"E117.MirrorCS"),sQuery(id+"F9.wireOp",EDGE,"E130.MirrorCS"),sQuery(id+"F9.wireOp",EDGE,"E140.MirrorCS")])],"isStart":true});
            var Q29;
            Q29=makeQuery(id+"F10.opExtrude","CAP_FACE",FACE,{"disambiguationData":[OSD([sQuery(id+"F9.wireOp",EDGE,"E112.MirrorCS"),sQuery(id+"F9.wireOp",EDGE,"E124.MirrorCS"),sQuery(id+"F9.wireOp",EDGE,"E138.MirrorCS")])],"isStart":true});
            var Q30;
            Q30=makeQuery(id+"F10.opExtrude","CAP_FACE",FACE,{"disambiguationData":[OSD([sQuery(id+"F9.wireOp",EDGE,"E115.MirrorCS"),sQuery(id+"F9.wireOp",EDGE,"E125.MirrorCS"),sQuery(id+"F9.wireOp",EDGE,"E143.MirrorCS")])],"isStart":true});
            var Q31;
            Q31=makeQuery(id+"F10.opExtrude","CAP_FACE",FACE,{"disambiguationData":[OSD([sQuery(id+"F9.wireOp",EDGE,"E127.MirrorCS"),sQuery(id+"F9.wireOp",EDGE,"E135.MirrorCS"),sQuery(id+"F9.wireOp",EDGE,"E142.MirrorCS")])],"isStart":true});
            var Q32;
            Q32=makeQuery(id+"F10.opExtrude","CAP_FACE",FACE,{"disambiguationData":[OSD([sQuery(id+"F9.wireOp",EDGE,"E121.MirrorCS"),sQuery(id+"F9.wireOp",EDGE,"E123.MirrorCS"),sQuery(id+"F9.wireOp",EDGE,"E144.MirrorCS")])],"isStart":true});
            var Q33;
            Q33=makeQuery(id+"F10.opExtrude","CAP_FACE",FACE,{"disambiguationData":[OSD([sQuery(id+"F9.wireOp",EDGE,"E126.MirrorCS"),sQuery(id+"F9.wireOp",EDGE,"E131.MirrorCS"),sQuery(id+"F9.wireOp",EDGE,"E133.MirrorCS")])],"isStart":true});
            var Q34;
            Q34=makeQuery(id+"F10.opExtrude","CAP_FACE",FACE,{"disambiguationData":[OSD([sQuery(id+"F9.wireOp",EDGE,"E111.MirrorCS"),sQuery(id+"F9.wireOp",EDGE,"E132.MirrorCS"),sQuery(id+"F9.wireOp",EDGE,"E141.MirrorCS")])],"isStart":true});
            var Q35;
            Q35=makeQuery(id+"F10.opExtrude","CAP_FACE",FACE,{"disambiguationData":[OSD([sQuery(id+"F9.wireOp",EDGE,"E116.MirrorCS"),sQuery(id+"F9.wireOp",EDGE,"E122.MirrorCS"),sQuery(id+"F9.wireOp",EDGE,"E134.MirrorCS")])],"isStart":true});
            var Q36;
            Q36=makeQuery(id+"F10.opExtrude","CAP_FACE",FACE,{"disambiguationData":[OSD([sQuery(id+"F9.wireOp",EDGE,"E102.MirrorCS"),sQuery(id+"F9.wireOp",EDGE,"E103.MirrorCS"),sQuery(id+"F9.wireOp",EDGE,"E104.MirrorCS")])],"isStart":true});
            var Q37;
            Q37=makeQuery(id+"F10.opExtrude","CAP_FACE",FACE,{"disambiguationData":[OSD([sQuery(id+"F9.wireOp",EDGE,"E105.MirrorCS"),sQuery(id+"F9.wireOp",EDGE,"E106.MirrorCS"),sQuery(id+"F9.wireOp",EDGE,"E107.MirrorCS")])],"isStart":true});
            var Q38;
            Q38=makeQuery(id+"F10.opExtrude","CAP_FACE",FACE,{"disambiguationData":[OSD([sQuery(id+"F9.wireOp",EDGE,"E91.MirrorCS"),sQuery(id+"F9.wireOp",EDGE,"E92.MirrorCS"),sQuery(id+"F9.wireOp",EDGE,"E95.MirrorCS")])],"isStart":true});
            var Q39;
            Q39=makeQuery(id+"F10.opExtrude","CAP_FACE",FACE,{"disambiguationData":[OSD([sQuery(id+"F9.wireOp",EDGE,"E90.MirrorCS"),sQuery(id+"F9.wireOp",EDGE,"E93.MirrorCS"),sQuery(id+"F9.wireOp",EDGE,"E94.MirrorCS")])],"isStart":true});
            var Q40;
            Q40=makeQuery(id+"F10.opExtrude","CAP_FACE",FACE,{"disambiguationData":[OSD([sQuery(id+"F9.wireOp",EDGE,"E96.MirrorCS"),sQuery(id+"F9.wireOp",EDGE,"E97.MirrorCS"),sQuery(id+"F9.wireOp",EDGE,"E98.MirrorCS")])],"isStart":true});
            var Q41;
            Q41=makeQuery(id+"F10.opExtrude","CAP_FACE",FACE,{"disambiguationData":[OSD([sQuery(id+"F9.wireOp",EDGE,"E99.MirrorCS"),sQuery(id+"F9.wireOp",EDGE,"E100.MirrorCS"),sQuery(id+"F9.wireOp",EDGE,"E101.MirrorCS")])],"isStart":true});
            var Q42;
            Q42=makeQuery(id+"F10.opExtrude","CAP_FACE",FACE,{"disambiguationData":[OSD([sQuery(id+"F9.wireOp",EDGE,"E74"),sQuery(id+"F9.wireOp",EDGE,"E75"),sQuery(id+"F9.wireOp",EDGE,"E76")])],"isStart":true});
            var Q43;
            Q43=makeQuery(id+"F10.opExtrude","CAP_FACE",FACE,{"disambiguationData":[OSD([sQuery(id+"F9.wireOp",EDGE,"E77"),sQuery(id+"F9.wireOp",EDGE,"E78"),sQuery(id+"F9.wireOp",EDGE,"E79")])],"isStart":true});
            var Q44;
            Q44=makeQuery(id+"F10.opExtrude","CAP_FACE",FACE,{"disambiguationData":[OSD([sQuery(id+"F9.wireOp",EDGE,"E80"),sQuery(id+"F9.wireOp",EDGE,"E81"),sQuery(id+"F9.wireOp",EDGE,"E82")])],"isStart":true});
            var Q45;
            Q45=makeQuery(id+"F10.opExtrude","CAP_FACE",FACE,{"disambiguationData":[OSD([sQuery(id+"F9.wireOp",EDGE,"E71"),sQuery(id+"F9.wireOp",EDGE,"E72"),sQuery(id+"F9.wireOp",EDGE,"E73")])],"isStart":true});
            var Q46;
            Q46=makeQuery(id+"F10.opExtrude","CAP_FACE",FACE,{"disambiguationData":[OSD([sQuery(id+"F9.wireOp",EDGE,"E84.MirrorCS"),sQuery(id+"F9.wireOp",EDGE,"E85.MirrorCS"),sQuery(id+"F9.wireOp",EDGE,"E86.MirrorCS")])],"isStart":true});
            var Q47;
            Q47=makeQuery(id+"F10.opExtrude","CAP_FACE",FACE,{"disambiguationData":[OSD([sQuery(id+"F9.wireOp",EDGE,"E87.MirrorCS"),sQuery(id+"F9.wireOp",EDGE,"E88.MirrorCS"),sQuery(id+"F9.wireOp",EDGE,"E89.MirrorCS")])],"isStart":true});
            extrude(context, id + "F11", {"entities" : qUnion([Q0, Q1, Q2, Q3, Q4, Q5, Q6, Q7, Q8, Q9, Q10, Q11, Q12, Q13, Q14, Q15, Q16, Q17, Q18, Q19, Q20, Q21, Q22, Q23, Q24, Q25, Q26, Q27, Q28, Q29, Q30, Q31, Q32, Q33, Q34, Q35, Q36, Q37, Q38, Q39, Q40, Q41, Q42, Q43, Q44, Q45, Q46, Q47]), "operationType" : NewBodyOperationType.REMOVE, "oppositeDirection" : true, "depth" : 12.7 * mm, "offsetDistance" : 25.4 * mm, "hasSecondDirection" : true, "secondDirectionOppositeDirection" : false, "secondDirectionDepth" : 12.7 * mm});
        }
    });
